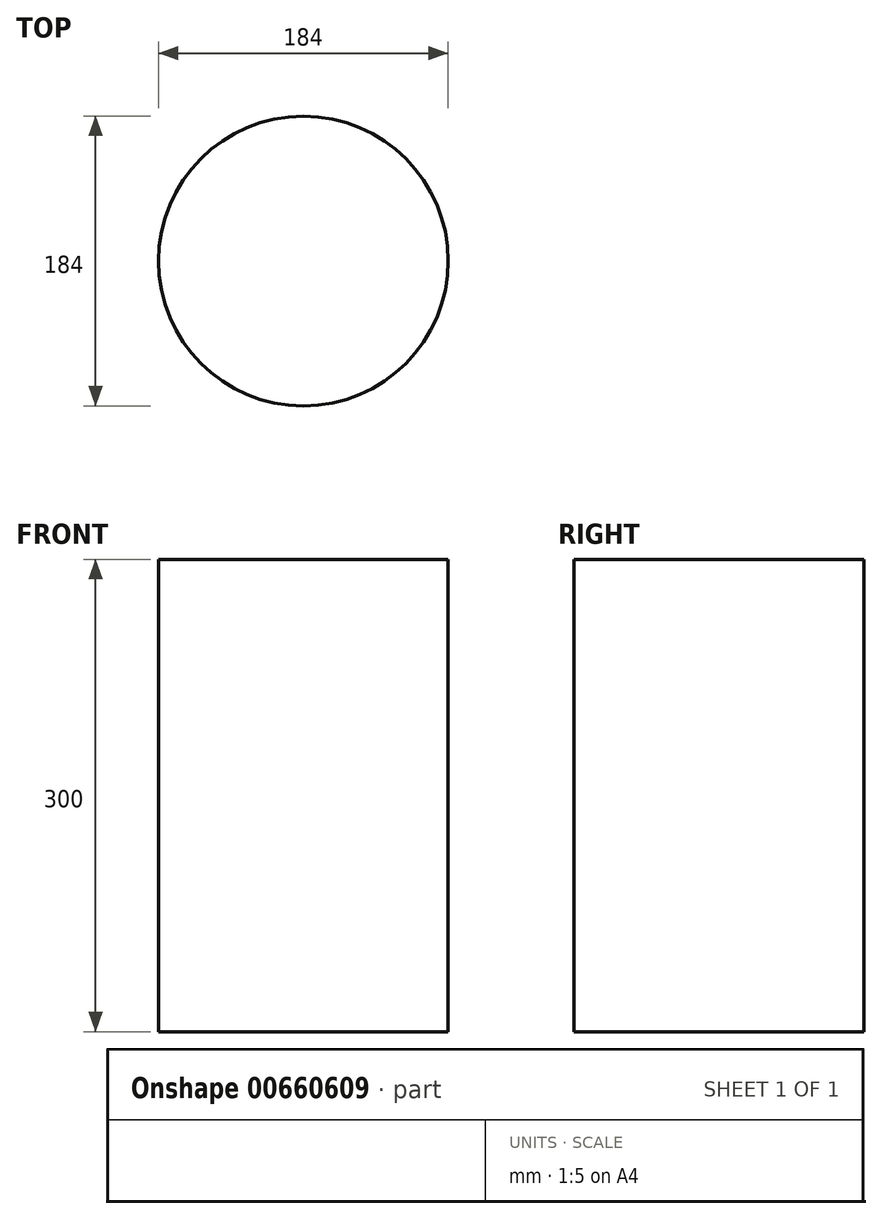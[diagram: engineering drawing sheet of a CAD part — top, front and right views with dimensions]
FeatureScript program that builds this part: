
annotation { "Feature Type Name" : "Feature", "Feature Type Description" : "" }
export const myFeature = defineFeature(function(context is Context, id is Id, definition is map)
    precondition{}
    {
        {
            var Q0;
            Q0=qCreatedBy(makeId("Top.planeOp"),FACE);
            cPlane(context, id + "F0", {"entities" : qUnion([Q0]), "cplaneType" : CPlaneType.OFFSET, "offset" : 100 * mm, "oppositeDirection" : true, "width" : 150 * mm, "height" : 150 * mm});
        }
        {
            var Q0;
            Q0=qCreatedBy(id+"F0.planeOp",FACE);
            var sketch = newSketch(context, id + "F1", { "sketchPlane" : qUnion([Q0])});
            skCircle(sketch, "E0", {"center": v(0, 0) * mm, "radius": 92 * mm});
            skSolve(sketch);
        }
        {
            var Q0;
            Q0=makeQuery(id+"F1.imprint","IMPRINT",FACE,{"disambiguationData":[TD([[makeQuery(id+"F1.imprint","IMPRINT",EDGE,{"derivedFrom":sQuery(id+"F1.wireOp",EDGE,"E0")}),1.0]])]});
            extrude(context, id + "F2", {"entities" : qUnion([Q0]), "oppositeDirection" : true, "depth" : 300 * mm, "offsetDistance" : 25 * mm});
        }
    });
